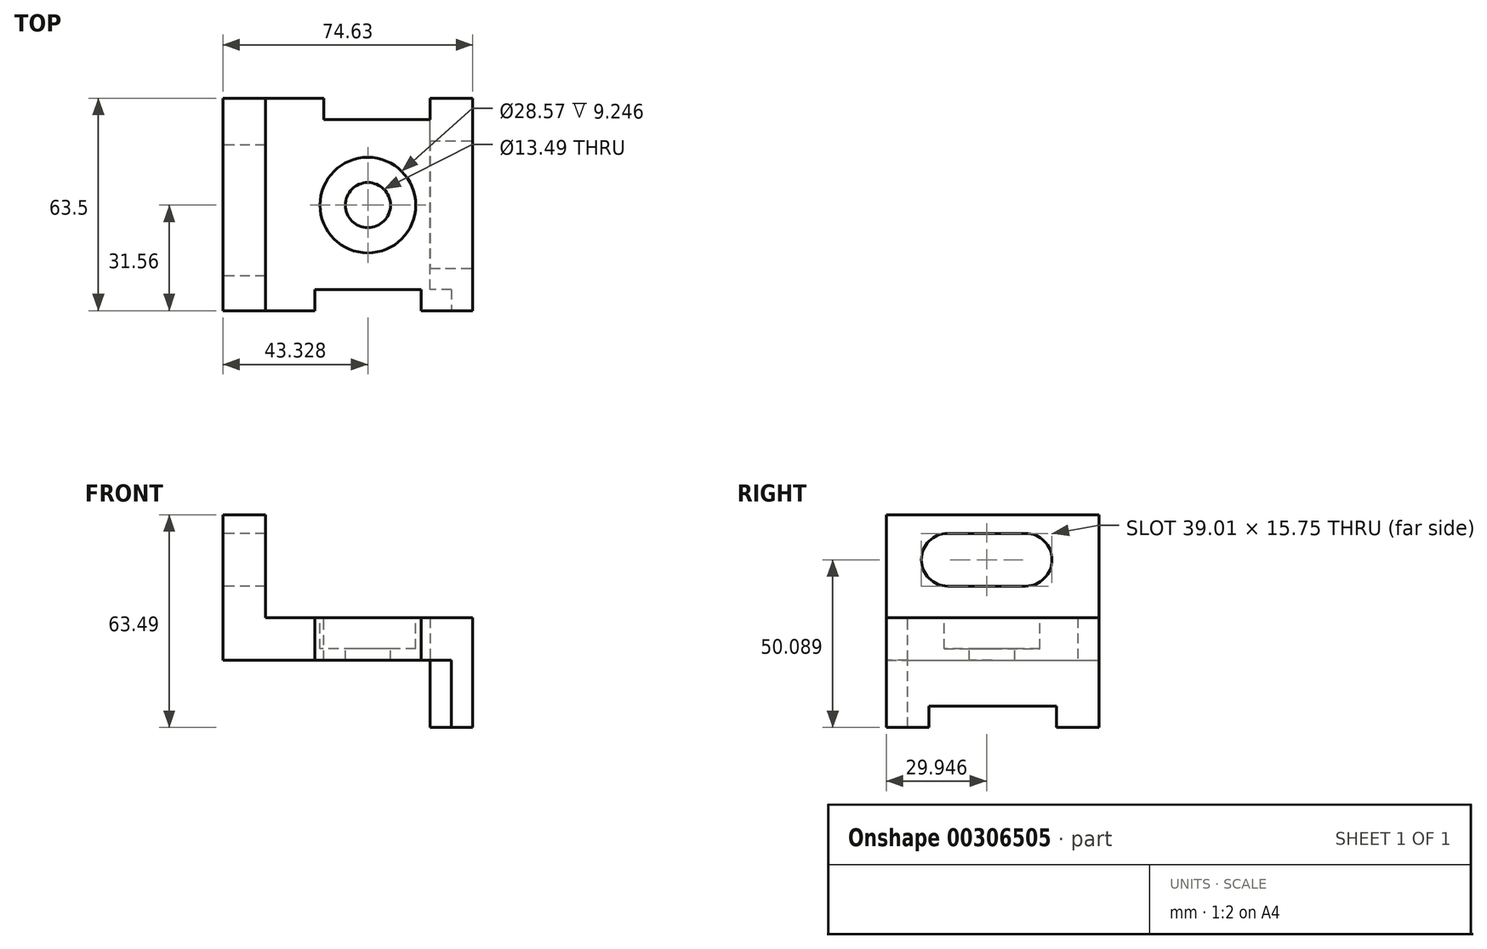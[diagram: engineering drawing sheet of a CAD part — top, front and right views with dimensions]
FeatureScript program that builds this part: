
annotation { "Feature Type Name" : "Feature", "Feature Type Description" : "" }
export const myFeature = defineFeature(function(context is Context, id is Id, definition is map)
    precondition{}
    {
        {
            var Q0;
            Q0=qCreatedBy(makeId("Front.planeOp"),FACE);
            var sketch = newSketch(context, id + "F0", { "sketchPlane" : qUnion([Q0])});
            skLineSegment(sketch, "E0", {"start": v(0, 0) * mm, "end": v(0, 43.47) * mm});
            skLineSegment(sketch, "E1", {"start": v(0, 43.47) * mm, "end": v(12.7, 43.47) * mm});
            skLineSegment(sketch, "E2", {"start": v(12.7, 43.47) * mm, "end": v(12.7, 12.7) * mm});
            skLineSegment(sketch, "E3", {"start": v(12.7, 12.7) * mm, "end": v(30.18, 12.7) * mm});
            skLineSegment(sketch, "E4", {"start": v(30.18, 12.7) * mm, "end": v(61.93, 12.7) * mm});
            skLineSegment(sketch, "E5", {"start": v(61.93, 12.7) * mm, "end": v(74.63, 12.7) * mm});
            skLineSegment(sketch, "E6", {"start": v(74.63, 12.7) * mm, "end": v(74.63, -20.02) * mm});
            skLineSegment(sketch, "E7", {"start": v(74.63, -20.02) * mm, "end": v(61.93, -20.02) * mm});
            skLineSegment(sketch, "E8", {"start": v(61.93, -20.02) * mm, "end": v(61.93, 0) * mm});
            skLineSegment(sketch, "E9", {"start": v(61.93, 0) * mm, "end": v(0, 0) * mm});
            skSolve(sketch);
        }
        {
            var Q0;
            Q0 = qSketchRegion(id + "F0", true);
            extrude(context, id + "F1", {"entities" : qUnion([Q0]), "depth" : 63.5 * mm});
        }
        {
            var Q0;
            Q0=makeQuery(id+"F1.opExtrude","CAP_FACE",FACE,{"disambiguationData":[OSD([sQuery(id+"F0.wireOp",EDGE,"E0"),sQuery(id+"F0.wireOp",EDGE,"E1"),sQuery(id+"F0.wireOp",EDGE,"E2"),sQuery(id+"F0.wireOp",EDGE,"E3"),sQuery(id+"F0.wireOp",EDGE,"E4"),sQuery(id+"F0.wireOp",EDGE,"E5"),sQuery(id+"F0.wireOp",EDGE,"E6"),sQuery(id+"F0.wireOp",EDGE,"E7"),sQuery(id+"F0.wireOp",EDGE,"E8"),sQuery(id+"F0.wireOp",EDGE,"E9")])],"isStart":false});
            var sketch = newSketch(context, id + "F2", { "sketchPlane" : qUnion([Q0])});
            skLineSegment(sketch, "E10.bottom", {"start": v(27.45, 0) * mm, "end": v(59.2, 0) * mm});
            skLineSegment(sketch, "E10.top", {"start": v(27.45, 12.7) * mm, "end": v(59.2, 12.7) * mm});
            skLineSegment(sketch, "E10.left", {"start": v(27.45, 0) * mm, "end": v(27.45, 12.7) * mm});
            skLineSegment(sketch, "E10.right", {"start": v(59.2, 0) * mm, "end": v(59.2, 12.7) * mm});
            skLineSegment(sketch, "E11.bottom", {"start": v(61.93, 0) * mm, "end": v(68.28, 0) * mm});
            skLineSegment(sketch, "E11.top", {"start": v(61.93, -20.02) * mm, "end": v(68.28, -20.02) * mm});
            skLineSegment(sketch, "E11.left", {"start": v(61.93, 0) * mm, "end": v(61.93, -20.02) * mm});
            skLineSegment(sketch, "E11.right", {"start": v(68.28, 0) * mm, "end": v(68.28, -20.02) * mm});
            skSolve(sketch);
        }
        {
            var Q0;
            Q0 = qSketchRegion(id + "F2", true);
            extrude(context, id + "F3", {"entities" : qUnion([Q0]), "operationType" : NewBodyOperationType.REMOVE, "endBound" : BoundingType.SYMMETRIC, "oppositeDirection" : true, "depth" : 12.7 * mm});
        }
        {
            var Q0;
            Q0=makeQuery(id+"F1.opExtrude","SWEPT_FACE",FACE,{"disambiguationData":[OSD([sQuery(id+"F0.wireOp",EDGE,"E6")])]});
            var sketch = newSketch(context, id + "F4", { "sketchPlane" : qUnion([Q0])});
            skLineSegment(sketch, "E12.bottom", {"start": v(-50.8, -20.02) * mm, "end": v(-12.7, -20.02) * mm});
            skLineSegment(sketch, "E12.top", {"start": v(-50.8, -13.67) * mm, "end": v(-12.7, -13.67) * mm});
            skLineSegment(sketch, "E12.left", {"start": v(-50.8, -20.02) * mm, "end": v(-50.8, -13.67) * mm});
            skLineSegment(sketch, "E12.right", {"start": v(-12.7, -20.02) * mm, "end": v(-12.7, -13.67) * mm});
            skSolve(sketch);
        }
        {
            var Q0;
            Q0 = qSketchRegion(id + "F4", true);
            extrude(context, id + "F5", {"entities" : qUnion([Q0]), "operationType" : NewBodyOperationType.REMOVE, "endBound" : BoundingType.THROUGH_ALL, "oppositeDirection" : true, "depth" : 25.4 * mm});
        }
        {
            var Q0;
            Q0=qCreatedBy(makeId("Right.planeOp"),FACE);
            var sketch = newSketch(context, id + "F6", { "sketchPlane" : qUnion([Q0])});
            skLineSegment(sketch, "E13", {"start": v(-45.19, 37.94) * mm, "end": v(-21.92, 37.94) * mm});
            skLineSegment(sketch, "E14", {"start": v(-45.19, 22.2) * mm, "end": v(-21.92, 22.2) * mm});
            skArc(sketch, "E15", {"start": v(-45.19, 37.94) * mm, "mid": v(-53.06, 30.07) * mm, "end": v(-45.19, 22.2) * mm});
            skArc(sketch, "E16", {"start": v(-21.92, 22.2) * mm, "mid": v(-14.05, 30.07) * mm, "end": v(-21.92, 37.94) * mm});
            skSolve(sketch);
        }
        {
            var Q0;
            Q0 = qSketchRegion(id + "F6", true);
            extrude(context, id + "F7", {"entities" : qUnion([Q0]), "operationType" : NewBodyOperationType.REMOVE, "endBound" : BoundingType.THROUGH_ALL, "depth" : 25.4 * mm});
        }
        {
            var Q0;
            Q0=makeQuery(id+"F1.opExtrude","SWEPT_FACE",FACE,{"disambiguationData":[OSD([sQuery(id+"F0.wireOp",EDGE,"E3"),sQuery(id+"F0.wireOp",EDGE,"E4"),sQuery(id+"F0.wireOp",EDGE,"E5")])]});
            var sketch = newSketch(context, id + "F8", { "sketchPlane" : qUnion([Q0])});
            skCircle(sketch, "E17", {"center": v(43.33, -31.94) * mm, "radius": 6.74 * mm});
            skPoint(sketch, "E17.centerSnap0", {"position": v(43.33, -57.15) * mm});
            skCircle(sketch, "E18", {"center": v(43.33, -31.94) * mm, "radius": 14.29 * mm});
            skSolve(sketch);
        }
        {
            var Q0;
            Q0=makeQuery(id+"F8.imprint","IMPRINT",FACE,{"disambiguationData":[TD([[makeQuery(id+"F8.imprint","IMPRINT",EDGE,{"derivedFrom":sQuery(id+"F8.wireOp",EDGE,"E17")}),1.0]])]});
            var Q1;
            Q1=makeQuery(id+"F8.imprint","IMPRINT",FACE,{"disambiguationData":[TD([[makeQuery(id+"F8.imprint","IMPRINT",EDGE,{"derivedFrom":sQuery(id+"F8.wireOp",EDGE,"E17")}),-1.0]])]});
            var Q2;
            Q2=sQuery(id+"F8.wireOp",EDGE,"E17");
            extrude(context, id + "F9", {"entities" : qUnion([Q0, Q1]), "operationType" : NewBodyOperationType.REMOVE, "surfaceEntities" : qUnion([Q2]), "oppositeDirection" : true, "depth" : 9.25 * mm});
        }
        {
            var Q0;
            Q0=makeQuery(id+"F9.boolean.opBoolean","COPY",FACE,{"derivedFrom":makeQuery(id+"F9.opExtrude","CAP_FACE",FACE,{"disambiguationData":[OSD([sQuery(id+"F8.wireOp",EDGE,"E18")])],"isStart":false})});
            var sketch = newSketch(context, id + "F10", { "sketchPlane" : qUnion([Q0])});
            skCircle(sketch, "E19", {"center": v(43.33, -31.94) * mm, "radius": 6.74 * mm});
            skSolve(sketch);
        }
        {
            var Q0;
            Q0 = qSketchRegion(id + "F10", true);
            extrude(context, id + "F11", {"entities" : qUnion([Q0]), "operationType" : NewBodyOperationType.REMOVE, "endBound" : BoundingType.THROUGH_ALL, "oppositeDirection" : true, "depth" : 25.4 * mm});
        }
        {
            var Q0;
            Q0=makeQuery(id+"F1.opExtrude","CAP_FACE",FACE,{"disambiguationData":[OSD([sQuery(id+"F0.wireOp",EDGE,"E0"),sQuery(id+"F0.wireOp",EDGE,"E1"),sQuery(id+"F0.wireOp",EDGE,"E2"),sQuery(id+"F0.wireOp",EDGE,"E3"),sQuery(id+"F0.wireOp",EDGE,"E4"),sQuery(id+"F0.wireOp",EDGE,"E5"),sQuery(id+"F0.wireOp",EDGE,"E6"),sQuery(id+"F0.wireOp",EDGE,"E7"),sQuery(id+"F0.wireOp",EDGE,"E8"),sQuery(id+"F0.wireOp",EDGE,"E9")])],"isStart":true});
            var sketch = newSketch(context, id + "F12", { "sketchPlane" : qUnion([Q0])});
            skLineSegment(sketch, "E20.bottom", {"start": v(-30.18, 12.7) * mm, "end": v(-61.93, 12.7) * mm});
            skLineSegment(sketch, "E20.left", {"start": v(-30.18, 12.7) * mm, "end": v(-30.18, 0) * mm});
            skLineSegment(sketch, "E20.right", {"start": v(-61.93, 12.7) * mm, "end": v(-61.93, 0) * mm});
            skLineSegment(sketch, "E21", {"start": v(-30.18, 0) * mm, "end": v(-61.93, 0) * mm});
            skSolve(sketch);
        }
        {
            var Q0;
            Q0 = qSketchRegion(id + "F12", true);
            extrude(context, id + "F13", {"entities" : qUnion([Q0]), "operationType" : NewBodyOperationType.REMOVE, "endBound" : BoundingType.SYMMETRIC, "oppositeDirection" : true, "depth" : 12.7 * mm});
        }
    });
